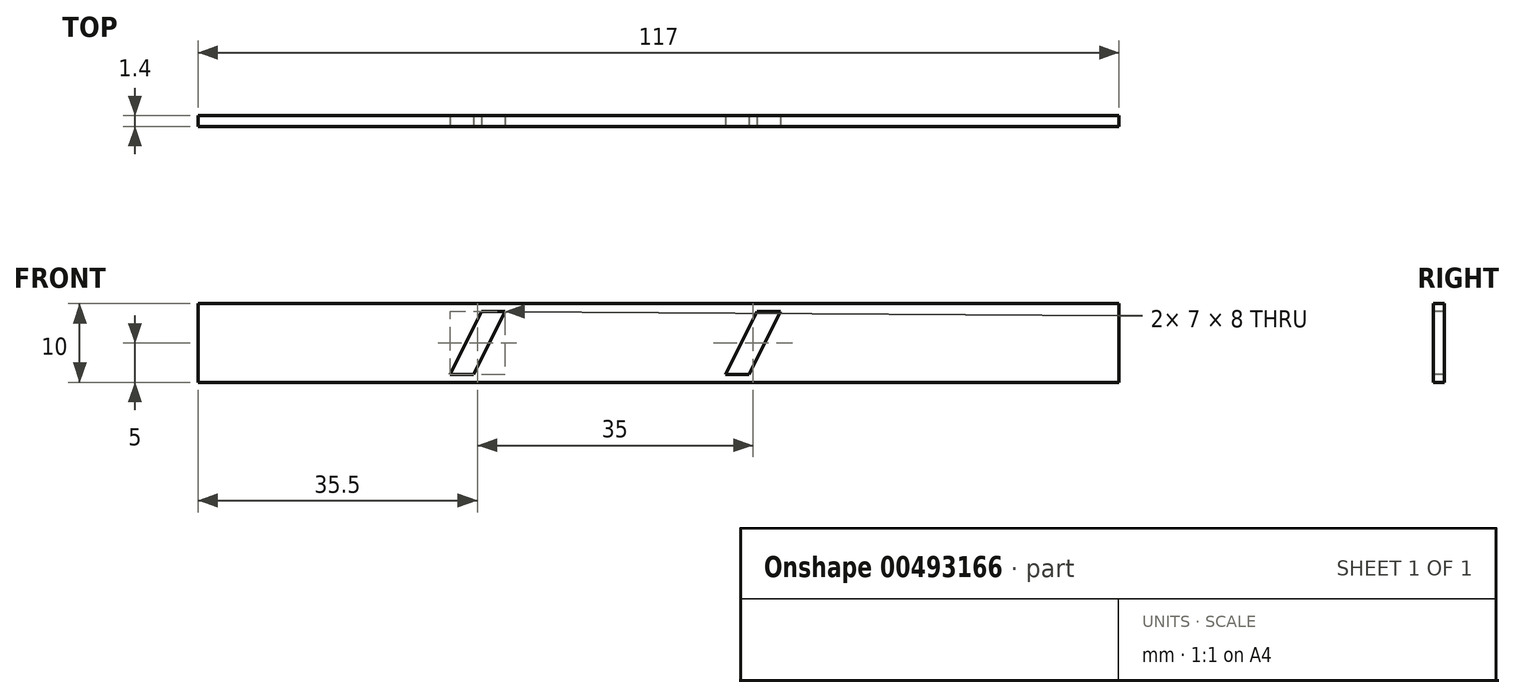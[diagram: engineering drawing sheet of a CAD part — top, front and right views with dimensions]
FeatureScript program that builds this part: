
annotation { "Feature Type Name" : "Feature", "Feature Type Description" : "" }
export const myFeature = defineFeature(function(context is Context, id is Id, definition is map)
    precondition{}
    {
        {
            var Q0;
            Q0=qCreatedBy(makeId("Front.planeOp"),FACE);
            var sketch = newSketch(context, id + "F0", { "sketchPlane" : qUnion([Q0])});
            skLineSegment(sketch, "E0.bottom", {"start": v(58.5, 5) * mm, "end": v(-58.5, 5) * mm});
            skLineSegment(sketch, "E0.top", {"start": v(58.5, -5) * mm, "end": v(-58.5, -5) * mm});
            skLineSegment(sketch, "E0.left", {"start": v(58.5, 5) * mm, "end": v(58.5, -5) * mm});
            skLineSegment(sketch, "E0.right", {"start": v(-58.5, 5) * mm, "end": v(-58.5, -5) * mm});
            skPoint(sketch, "E0.middle", {"position": v(0, 0) * mm});
            skSolve(sketch);
        }
        {
            var Q0;
            Q0 = qSketchRegion(id + "F0", true);
            extrude(context, id + "F1", {"entities" : qUnion([Q0]), "depth" : 1.4 * mm});
        }
        {
            var Q0;
            Q0=makeQuery(id+"F1.opExtrude","CAP_FACE",FACE,{"disambiguationData":[OSD([sQuery(id+"F0.wireOp",EDGE,"E0.bottom"),sQuery(id+"F0.wireOp",EDGE,"E0.top"),sQuery(id+"F0.wireOp",EDGE,"E0.left"),sQuery(id+"F0.wireOp",EDGE,"E0.right")])],"isStart":false});
            var sketch = newSketch(context, id + "F2", { "sketchPlane" : qUnion([Q0])});
            skLineSegment(sketch, "E1", {"start": v(-26.5, -4) * mm, "end": v(-23.5, -4) * mm});
            skLineSegment(sketch, "E2", {"start": v(8.5, -4) * mm, "end": v(11.5, -4) * mm});
            skLineSegment(sketch, "E3", {"start": v(-22.5, 4) * mm, "end": v(-19.5, 4) * mm});
            skLineSegment(sketch, "E4", {"start": v(12.5, 4) * mm, "end": v(15.5, 4) * mm});
            skLineSegment(sketch, "E5", {"start": v(-26.5, -4) * mm, "end": v(-22.5, 4) * mm});
            skLineSegment(sketch, "E6", {"start": v(-19.5, 4) * mm, "end": v(-23.5, -4) * mm});
            skLineSegment(sketch, "E7", {"start": v(12.5, 4) * mm, "end": v(8.5, -4) * mm});
            skLineSegment(sketch, "E8", {"start": v(15.5, 4) * mm, "end": v(11.5, -4) * mm});
            skSolve(sketch);
        }
        {
            var Q0;
            Q0 = qSketchRegion(id + "F2", true);
            extrude(context, id + "F3", {"entities" : qUnion([Q0]), "operationType" : NewBodyOperationType.REMOVE, "oppositeDirection" : true, "depth" : 25 * mm});
        }
    });
